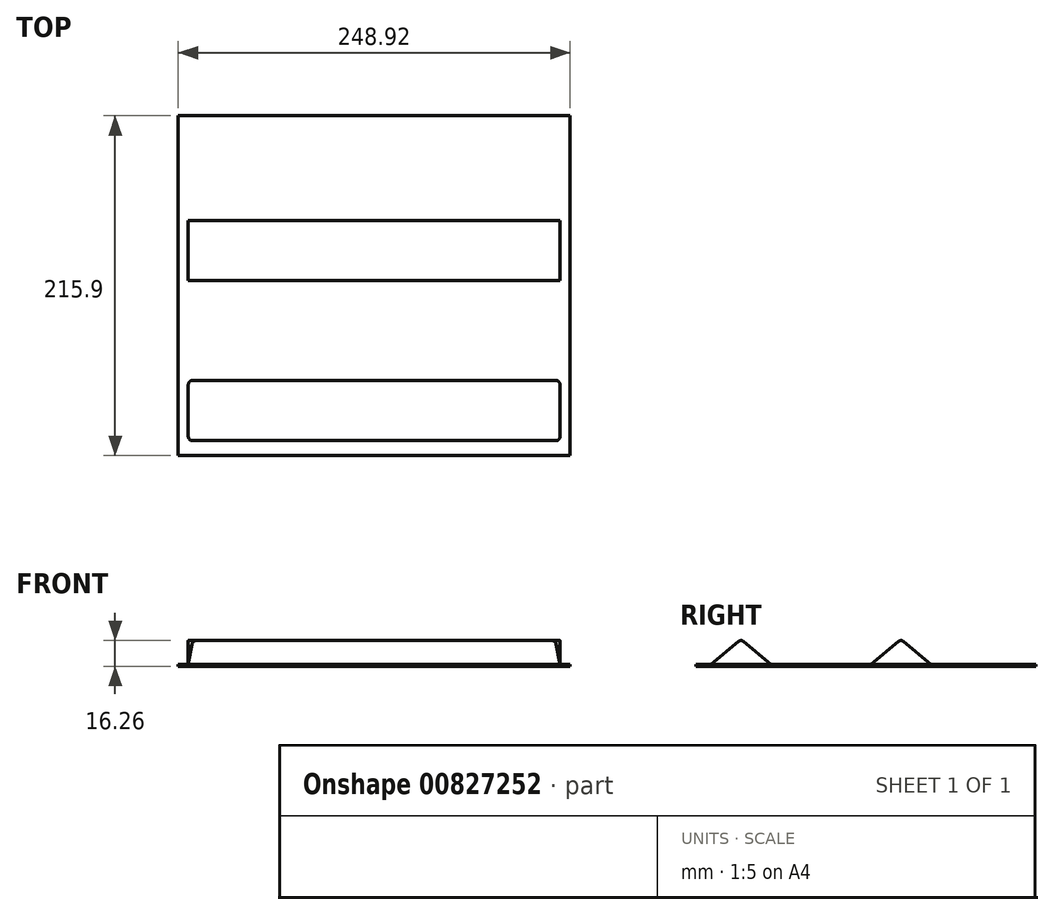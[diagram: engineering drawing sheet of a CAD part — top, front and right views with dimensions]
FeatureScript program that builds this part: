
annotation { "Feature Type Name" : "Feature", "Feature Type Description" : "" }
export const myFeature = defineFeature(function(context is Context, id is Id, definition is map)
    precondition{}
    {
        {
            var Q0;
            Q0=qCreatedBy(makeId("Top.planeOp"),FACE);
            var sketch = newSketch(context, id + "F0", { "sketchPlane" : qUnion([Q0])});
            skLineSegment(sketch, "E0.bottom", {"start": v(-124.46, -107.95) * mm, "end": v(124.46, -107.95) * mm});
            skLineSegment(sketch, "E0.top", {"start": v(-124.46, 107.95) * mm, "end": v(124.46, 107.95) * mm});
            skLineSegment(sketch, "E0.left", {"start": v(-124.46, -107.95) * mm, "end": v(-124.46, 107.95) * mm});
            skLineSegment(sketch, "E0.right", {"start": v(124.46, -107.95) * mm, "end": v(124.46, 107.95) * mm});
            skPoint(sketch, "E0.middle", {"position": v(0, 0) * mm});
            skSolve(sketch);
        }
        {
            var Q0;
            Q0=makeQuery(id+"F0.imprint","IMPRINT",FACE,{"disambiguationData":[TD([[makeQuery(id+"F0.imprint","IMPRINT",EDGE,{"derivedFrom":sQuery(id+"F0.wireOp",EDGE,"E0.bottom")}),1.0]])]});
            extrude(context, id + "F1", {"entities" : qUnion([Q0]), "depth" : 1.27 * mm, "offsetDistance" : 25.4 * mm});
        }
        {
            var Q0;
            Q0=qCreatedBy(makeId("Right.planeOp"),FACE);
            var sketch = newSketch(context, id + "F2", { "sketchPlane" : qUnion([Q0])});
            skLineSegment(sketch, "E1", {"start": v(-98.43, 1.27) * mm, "end": v(-60.33, 1.27) * mm});
            skLineSegment(sketch, "E2", {"start": v(-79.38, 17.02) * mm, "end": v(-98.43, 1.27) * mm});
            skLineSegment(sketch, "E3", {"start": v(-79.38, 17.02) * mm, "end": v(-60.33, 1.27) * mm});
            skPoint(sketch, "E4.start.orphan", {"position": v(-79.38, 1.27) * mm});
            skLineSegment(sketch, "E5", {"start": v(3.17, 1.27) * mm, "end": v(41.27, 1.27) * mm});
            skLineSegment(sketch, "E6", {"start": v(22.22, 17.02) * mm, "end": v(41.27, 1.27) * mm});
            skLineSegment(sketch, "E7", {"start": v(22.22, 17.02) * mm, "end": v(3.17, 1.27) * mm});
            skPoint(sketch, "E8.start.orphan", {"position": v(22.22, 1.27) * mm});
            skSolve(sketch);
        }
        {
            var Q0;
            Q0=makeQuery(id+"F2.imprint","IMPRINT",FACE,{"disambiguationData":[TD([[makeQuery(id+"F2.imprint","IMPRINT",EDGE,{"derivedFrom":sQuery(id+"F2.wireOp",EDGE,"E5")}),1.0]])]});
            var Q1;
            Q1=makeQuery(id+"F2.imprint","IMPRINT",FACE,{"disambiguationData":[TD([[makeQuery(id+"F2.imprint","IMPRINT",EDGE,{"derivedFrom":sQuery(id+"F2.wireOp",EDGE,"E1")}),1.0]])]});
            extrude(context, id + "F3", {"entities" : qUnion([Q0, Q1]), "operationType" : NewBodyOperationType.ADD, "endBound" : BoundingType.SYMMETRIC, "depth" : 236.22 * mm, "offsetDistance" : 25.4 * mm});
        }
        {
            var Q0;
            Q0=qCreatedBy(makeId("Top.planeOp"),FACE);
            cPlane(context, id + "F4", {"entities" : qUnion([Q0]), "cplaneType" : CPlaneType.OFFSET, "offset" : 17.02 * mm, "width" : 152.4 * mm, "height" : 152.4 * mm});
        }
        {
            var Q0;
            Q0=makeQuery(id+"F1.opExtrude","CAP_FACE",FACE,{"disambiguationData":[OSD([sQuery(id+"F0.wireOp",EDGE,"E0.bottom"),sQuery(id+"F0.wireOp",EDGE,"E0.top"),sQuery(id+"F0.wireOp",EDGE,"E0.left"),sQuery(id+"F0.wireOp",EDGE,"E0.right")])],"isStart":false});
            var sketch = newSketch(context, id + "F5", { "sketchPlane" : qUnion([Q0])});
            skLineSegment(sketch, "E9.bottom", {"start": v(-118.11, -60.33) * mm, "end": v(-124.46, -60.33) * mm});
            skLineSegment(sketch, "E9.top", {"start": v(-118.11, -98.89) * mm, "end": v(-124.46, -98.89) * mm});
            skLineSegment(sketch, "E9.left", {"start": v(-118.11, -60.33) * mm, "end": v(-118.11, -98.89) * mm});
            skLineSegment(sketch, "E9.right", {"start": v(-124.46, -60.33) * mm, "end": v(-124.46, -98.89) * mm});
            skSolve(sketch);
        }
        {
            var Q0;
            Q0=qCreatedBy(id+"F4.planeOp",FACE);
            var sketch = newSketch(context, id + "F6", { "sketchPlane" : qUnion([Q0])});
            skLineSegment(sketch, "E10.bottom", {"start": v(-114.94, -60.15) * mm, "end": v(-121.35, -60.15) * mm});
            skLineSegment(sketch, "E10.top", {"start": v(-114.94, -98.8) * mm, "end": v(-121.35, -98.8) * mm});
            skLineSegment(sketch, "E10.left", {"start": v(-114.94, -60.15) * mm, "end": v(-114.94, -98.8) * mm});
            skLineSegment(sketch, "E10.right", {"start": v(-121.35, -60.15) * mm, "end": v(-121.35, -98.8) * mm});
            skSolve(sketch);
        }
        {
            var Q1;
            Q1=makeQuery(id+"F6.imprint","IMPRINT",FACE,{"disambiguationData":[TD([[makeQuery(id+"F6.imprint","IMPRINT",EDGE,{"derivedFrom":sQuery(id+"F6.wireOp",EDGE,"E10.bottom")}),1.0]])]});
            var Q2;
            {var subQ4=sQuery(id+"F5.wireOp",EDGE,"E9.bottom");Q2=makeQuery(id+"F5.imprint","IMPRINT",FACE,{"disambiguationData":[TD([[makeQuery(id+"F5.imprint","IMPRINT",EDGE,{"derivedFrom":subQ4}),1.0]])]});}
            loft(context, id + "F7", {"operationType" : NewBodyOperationType.REMOVE, "sheetProfilesArray" : [{ "sheetProfileEntities" : qUnion([Q1]) }, { "sheetProfileEntities" : qUnion([Q2]) }]});
        }
        {
            var Q0;
            Q0=makeQuery(id+"F1.opExtrude","SWEPT_FACE",FACE,{"disambiguationData":[OSD([sQuery(id+"F0.wireOp",EDGE,"E0.bottom")])]});
            cPlane(context, id + "F8", {"entities" : qUnion([Q0]), "cplaneType" : CPlaneType.OFFSET, "offset" : 79.38 * mm, "oppositeDirection" : true, "width" : 152.4 * mm, "height" : 152.4 * mm});
        }
        {
            var Q0;
            Q0=makeQuery(id+"F1.opExtrude","CAP_FACE",FACE,{"disambiguationData":[OSD([sQuery(id+"F0.wireOp",EDGE,"E0.bottom"),sQuery(id+"F0.wireOp",EDGE,"E0.top"),sQuery(id+"F0.wireOp",EDGE,"E0.left"),sQuery(id+"F0.wireOp",EDGE,"E0.right")])],"isStart":false});
            var sketch = newSketch(context, id + "F9", { "sketchPlane" : qUnion([Q0])});
            skLineSegment(sketch, "E11.bottom", {"start": v(118.11, -60.33) * mm, "end": v(124.46, -60.33) * mm});
            skLineSegment(sketch, "E11.top", {"start": v(118.11, -99.37) * mm, "end": v(124.46, -99.37) * mm});
            skLineSegment(sketch, "E11.left", {"start": v(118.11, -60.33) * mm, "end": v(118.11, -99.37) * mm});
            skLineSegment(sketch, "E11.right", {"start": v(124.46, -60.33) * mm, "end": v(124.46, -99.37) * mm});
            skSolve(sketch);
        }
        {
            var Q0;
            Q0=qCreatedBy(id+"F4.planeOp",FACE);
            var sketch = newSketch(context, id + "F10", { "sketchPlane" : qUnion([Q0])});
            skLineSegment(sketch, "E12.bottom", {"start": v(114.94, -60.13) * mm, "end": v(120.84, -60.13) * mm});
            skLineSegment(sketch, "E12.top", {"start": v(114.94, -99.37) * mm, "end": v(120.84, -99.37) * mm});
            skLineSegment(sketch, "E12.left", {"start": v(114.94, -60.13) * mm, "end": v(114.94, -99.37) * mm});
            skLineSegment(sketch, "E12.right", {"start": v(120.84, -60.13) * mm, "end": v(120.84, -99.37) * mm});
            skSolve(sketch);
        }
        {
            var Q1;
            Q1=makeQuery(id+"F10.imprint","IMPRINT",FACE,{"disambiguationData":[TD([[makeQuery(id+"F10.imprint","IMPRINT",EDGE,{"derivedFrom":sQuery(id+"F10.wireOp",EDGE,"E12.bottom")}),-1.0]])]});
            var Q2;
            {var subQ4=sQuery(id+"F9.wireOp",EDGE,"E11.bottom");Q2=makeQuery(id+"F9.imprint","IMPRINT",FACE,{"disambiguationData":[TD([[makeQuery(id+"F9.imprint","IMPRINT",EDGE,{"derivedFrom":subQ4}),-1.0]])]});}
            loft(context, id + "F11", {"operationType" : NewBodyOperationType.REMOVE, "sheetProfilesArray" : [{ "sheetProfileEntities" : qUnion([Q1]) }, { "sheetProfileEntities" : qUnion([Q2]) }]});
        }
        {
            var Q0;
            Q0=makeQuery(id+"F3.opExtrude","SWEPT_EDGE",EDGE,{"disambiguationData":[OSD([sQuery(id+"F2.wireOp",EDGE,"E6"),sQuery(id+"F2.wireOp",EDGE,"E7")])]});
            var Q1;
            Q1=makeQuery(id+"FznyGHjdi5sJpHq_1.1.F7.boolean.opBoolean","INTERSECT",EDGE,{"derivedFrom":[makeQuery(id+"F3.opExtrude","SWEPT_FACE",FACE,{"disambiguationData":[OSD([sQuery(id+"F2.wireOp",EDGE,"E6")])]}),makeQuery(id+"FznyGHjdi5sJpHq_1.1.F7.opLoft","SWEPT_FACE",FACE,{"disambiguationData":[OSD([sQuery(id+"F2.wireOp",EDGE,"E1"),sQuery(id+"F2.wireOp",EDGE,"E2"),sQuery(id+"F2.wireOp",EDGE,"E3"),sQuery(id+"F5.wireOp",EDGE,"E9.bottom"),sQuery(id+"F5.wireOp",EDGE,"E9.left"),sQuery(id+"F6.wireOp",EDGE,"E10.bottom"),sQuery(id+"F6.wireOp",EDGE,"E10.left")])]})]});
            var Q2;
            Q2=makeQuery(id+"FznyGHjdi5sJpHq_1.1.F7.boolean.opBoolean","INTERSECT",EDGE,{"derivedFrom":[makeQuery(id+"F3.opExtrude","SWEPT_FACE",FACE,{"disambiguationData":[OSD([sQuery(id+"F2.wireOp",EDGE,"E7")])]}),makeQuery(id+"FznyGHjdi5sJpHq_1.1.F7.opLoft","SWEPT_FACE",FACE,{"disambiguationData":[OSD([sQuery(id+"F2.wireOp",EDGE,"E1"),sQuery(id+"F2.wireOp",EDGE,"E2"),sQuery(id+"F2.wireOp",EDGE,"E3"),sQuery(id+"F5.wireOp",EDGE,"E9.bottom"),sQuery(id+"F5.wireOp",EDGE,"E9.left"),sQuery(id+"F6.wireOp",EDGE,"E10.bottom"),sQuery(id+"F6.wireOp",EDGE,"E10.left")])]})]});
            var Q3;
            Q3=makeQuery(id+"F7Xys2EDdf574f9_1.1.F11.boolean.opBoolean","INTERSECT",EDGE,{"derivedFrom":[makeQuery(id+"F3.opExtrude","SWEPT_FACE",FACE,{"disambiguationData":[OSD([sQuery(id+"F2.wireOp",EDGE,"E6")])]}),makeQuery(id+"F7Xys2EDdf574f9_1.1.F11.opLoft","SWEPT_FACE",FACE,{"disambiguationData":[OSD([sQuery(id+"F2.wireOp",EDGE,"E1"),sQuery(id+"F2.wireOp",EDGE,"E2"),sQuery(id+"F2.wireOp",EDGE,"E3"),sQuery(id+"F9.wireOp",EDGE,"E11.bottom"),sQuery(id+"F9.wireOp",EDGE,"E11.left"),sQuery(id+"F10.wireOp",EDGE,"E12.bottom"),sQuery(id+"F10.wireOp",EDGE,"E12.top"),sQuery(id+"F10.wireOp",EDGE,"E12.left")])]})]});
            var Q4;
            Q4=makeQuery(id+"F7Xys2EDdf574f9_1.1.F11.boolean.opBoolean","INTERSECT",EDGE,{"derivedFrom":[makeQuery(id+"F3.opExtrude","SWEPT_FACE",FACE,{"disambiguationData":[OSD([sQuery(id+"F2.wireOp",EDGE,"E7")])]}),makeQuery(id+"F7Xys2EDdf574f9_1.1.F11.opLoft","SWEPT_FACE",FACE,{"disambiguationData":[OSD([sQuery(id+"F2.wireOp",EDGE,"E1"),sQuery(id+"F2.wireOp",EDGE,"E2"),sQuery(id+"F2.wireOp",EDGE,"E3"),sQuery(id+"F9.wireOp",EDGE,"E11.bottom"),sQuery(id+"F9.wireOp",EDGE,"E11.left"),sQuery(id+"F10.wireOp",EDGE,"E12.bottom"),sQuery(id+"F10.wireOp",EDGE,"E12.top"),sQuery(id+"F10.wireOp",EDGE,"E12.left")])]})]});
            var Q5;
            Q5=makeQuery(id+"F3.opExtrude","SWEPT_EDGE",EDGE,{"disambiguationData":[OSD([sQuery(id+"F2.wireOp",EDGE,"E5"),sQuery(id+"F2.wireOp",EDGE,"E7")])]});
            var Q6;
            Q6=makeQuery(id+"F7Xys2EDdf574f9_1.1.F11.boolean.opBoolean","MERGE",EDGE,{"derivedFrom":[makeQuery(id+"F3.opExtrude","CAP_EDGE",EDGE,{"disambiguationData":[OSD([sQuery(id+"F2.wireOp",EDGE,"E5")])],"isStart":false}),makeQuery(id+"F7Xys2EDdf574f9_1.1.F11.opLoft","MID_CAP_EDGE",EDGE,{"disambiguationData":[OSD([sQuery(id+"F2.wireOp",EDGE,"E1"),sQuery(id+"F2.wireOp",EDGE,"E2"),sQuery(id+"F2.wireOp",EDGE,"E3"),sQuery(id+"F9.wireOp",EDGE,"E11.bottom"),sQuery(id+"F9.wireOp",EDGE,"E11.left")])],"capPos":1.0})]});
            var Q7;
            Q7=makeQuery(id+"F3.opExtrude","SWEPT_EDGE",EDGE,{"disambiguationData":[OSD([sQuery(id+"F2.wireOp",EDGE,"E2"),sQuery(id+"F2.wireOp",EDGE,"E3")])]});
            var Q8;
            {var subQ0=sQuery(id+"F2.wireOp",EDGE,"E3");Q8=makeQuery(id+"F7.boolean.opBoolean","INTERSECT",EDGE,{"derivedFrom":[makeQuery(id+"F3.opExtrude","SWEPT_FACE",FACE,{"disambiguationData":[OSD([subQ0])]}),makeQuery(id+"F7.opLoft","SWEPT_FACE",FACE,{"disambiguationData":[OSD([sQuery(id+"F2.wireOp",EDGE,"E1"),sQuery(id+"F2.wireOp",EDGE,"E2"),subQ0,sQuery(id+"F5.wireOp",EDGE,"E9.bottom"),sQuery(id+"F5.wireOp",EDGE,"E9.left"),sQuery(id+"F6.wireOp",EDGE,"E10.bottom"),sQuery(id+"F6.wireOp",EDGE,"E10.left")])]})]});}
            var Q9;
            {var subQ0=sQuery(id+"F2.wireOp",EDGE,"E2");Q9=makeQuery(id+"F7.boolean.opBoolean","INTERSECT",EDGE,{"derivedFrom":[makeQuery(id+"F3.opExtrude","SWEPT_FACE",FACE,{"disambiguationData":[OSD([subQ0])]}),makeQuery(id+"F7.opLoft","SWEPT_FACE",FACE,{"disambiguationData":[OSD([sQuery(id+"F2.wireOp",EDGE,"E1"),subQ0,sQuery(id+"F2.wireOp",EDGE,"E3"),sQuery(id+"F5.wireOp",EDGE,"E9.bottom"),sQuery(id+"F5.wireOp",EDGE,"E9.left"),sQuery(id+"F6.wireOp",EDGE,"E10.bottom"),sQuery(id+"F6.wireOp",EDGE,"E10.left")])]})]});}
            var Q10;
            {var subQ0=sQuery(id+"F2.wireOp",EDGE,"E2");Q10=makeQuery(id+"F11.boolean.opBoolean","INTERSECT",EDGE,{"derivedFrom":[makeQuery(id+"F3.opExtrude","SWEPT_FACE",FACE,{"disambiguationData":[OSD([subQ0])]}),makeQuery(id+"F11.opLoft","SWEPT_FACE",FACE,{"disambiguationData":[OSD([sQuery(id+"F2.wireOp",EDGE,"E1"),subQ0,sQuery(id+"F2.wireOp",EDGE,"E3"),sQuery(id+"F9.wireOp",EDGE,"E11.bottom"),sQuery(id+"F9.wireOp",EDGE,"E11.left"),sQuery(id+"F10.wireOp",EDGE,"E12.bottom"),sQuery(id+"F10.wireOp",EDGE,"E12.top"),sQuery(id+"F10.wireOp",EDGE,"E12.left")])]})]});}
            var Q11;
            {var subQ0=sQuery(id+"F2.wireOp",EDGE,"E3");Q11=makeQuery(id+"F11.boolean.opBoolean","INTERSECT",EDGE,{"derivedFrom":[makeQuery(id+"F3.opExtrude","SWEPT_FACE",FACE,{"disambiguationData":[OSD([subQ0])]}),makeQuery(id+"F11.opLoft","SWEPT_FACE",FACE,{"disambiguationData":[OSD([sQuery(id+"F2.wireOp",EDGE,"E1"),sQuery(id+"F2.wireOp",EDGE,"E2"),subQ0,sQuery(id+"F9.wireOp",EDGE,"E11.bottom"),sQuery(id+"F9.wireOp",EDGE,"E11.left"),sQuery(id+"F10.wireOp",EDGE,"E12.bottom"),sQuery(id+"F10.wireOp",EDGE,"E12.top"),sQuery(id+"F10.wireOp",EDGE,"E12.left")])]})]});}
            var Q12;
            Q12=makeQuery(id+"F3.opExtrude","SWEPT_EDGE",EDGE,{"disambiguationData":[OSD([sQuery(id+"F2.wireOp",EDGE,"E1"),sQuery(id+"F2.wireOp",EDGE,"E3")])]});
            fillet(context, id + "F12", {"entities" : qUnion([Q0, Q1, Q2, Q3, Q4, Q5, Q6, Q7, Q8, Q9, Q10, Q11, Q12]), "radius" : 2.54 * mm, "tangentPropagation" : true, "allowEdgeOverflow" : false});
        }
    });
